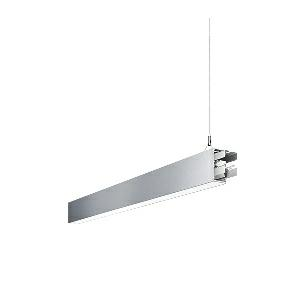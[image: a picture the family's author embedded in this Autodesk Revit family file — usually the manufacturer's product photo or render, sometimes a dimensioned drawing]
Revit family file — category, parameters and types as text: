
# Revit family: dotoo_line_-_dlp_1000_830_d_mid_00805841_0438
name_source: partatom
category: Lighting Fixtures
units: mm (PartAtom-declared; Revit-internal decimal feet)

## family parameters
Cut with Voids When Loaded = No
Host = Face
Light Source = No
Part Type = Normal
Room Calculation Point = No
Round Connector Dimension = Use Diameter
Shared = No

## types (1)
- DOTOO.line - DLP 1000/830/D MID (1 x LED, 1000 lm, 3000K)
    Apparent Load = 10 VA
    Approval mark = CE
    CIE Flux Codes = 67 91 98 100 100
    Color Rendering = 80-89
    Color Temperature = 3000K
    Control Gear = Electronic ballast
    Default Elevation = 1800 mm
    Description = DLP 1000/830/D|Suspended luminaire|light source: LED|connected load: 220-240 V, 50/60 Hz|Power consumption: approx. 10 W|standby: approx. 0,20|luminous flux: 1000 lm|luminous efficacy: 100 lm/W|light distribution: Direct|direct ratio: approx. 100 %|colour temperature: Warm white, ca. 3000 K|color rendering index (CRI): >= 80|chromaticity tolerance:  3 SDCM|System of protection: IP 40|technology: Continuously dimmable|luminaire body|material: Sectional aluminium|colour: Silver|lamp cover: Acrylic (PMMA), Clear|mains lead: 1,0 m With free stranded wires|Fastening: Steel cable 0.3 - 0.7 m|glare control: Prism aperture|luminance(L65): <= 3000 cd/m|unified glare rating(4H 8H): <=  19|special features: DALI Load 1x, TouchDIM - dimming via standard switch, Through-wired, up to 18 m on one mains connection, Flicker-free, Suitable as emergency lighting, Mechanical and electrical connection of the individual modules without tools|
    Frequency = 50 Hz
    Height = 110 mm
    Lamp = 1 x LED
    Lamp Light Flux = 1000 lm
    Lamp count = 1
    Length = 842 mm
    Luminous efficacy = 100 lm/W
    Manufacturer = Waldmann
    ModVariant = No
    Model = 00805841
    Mounting Place = Ceiling
    Mounting Type = Pendant
    Number of Poles = 1
    OnlyDefault = Yes
    Power Factor = 1
    Product Name = DOTOO.line - DLP 1000/830/D MID
    Product group = Suspended luminaire
    ProductGroupID = 9
    Protection Class = Protection class I
    Protection Degree = IP 40
    RLX_Detail_Level = 1
    RLX_Emergency_Light_Flux = 0 lm
    RLX_Emergency_Type = 0
    RLX_Emergency_Type_DB = No
    RlxData = <blob elided: 19589 chars, md5=69c3b95f>
    Socket = socket
    Standby Power = 0 W
    System Light Flux = 1000 lm
    System Power = 10 W
    Type Comments = Product without accessories
    Type Image = 113299000-00692561.jpg
    URL = http://relux.com
    VarID = ---
    Voltage = 230 V
    Voltage Range = 220-240 V
    Weight = 0.00 kg
    Width = 60 mm  [stored 0.19685 ft]

note: [stored X ft] marks values corroborated as IEEE doubles in the binary element streams (Revit-internal decimal feet)

## geometry (parser evidence)
native form markers: Blend x4, Sweep x11
no freeform markers — native parametric forms only
